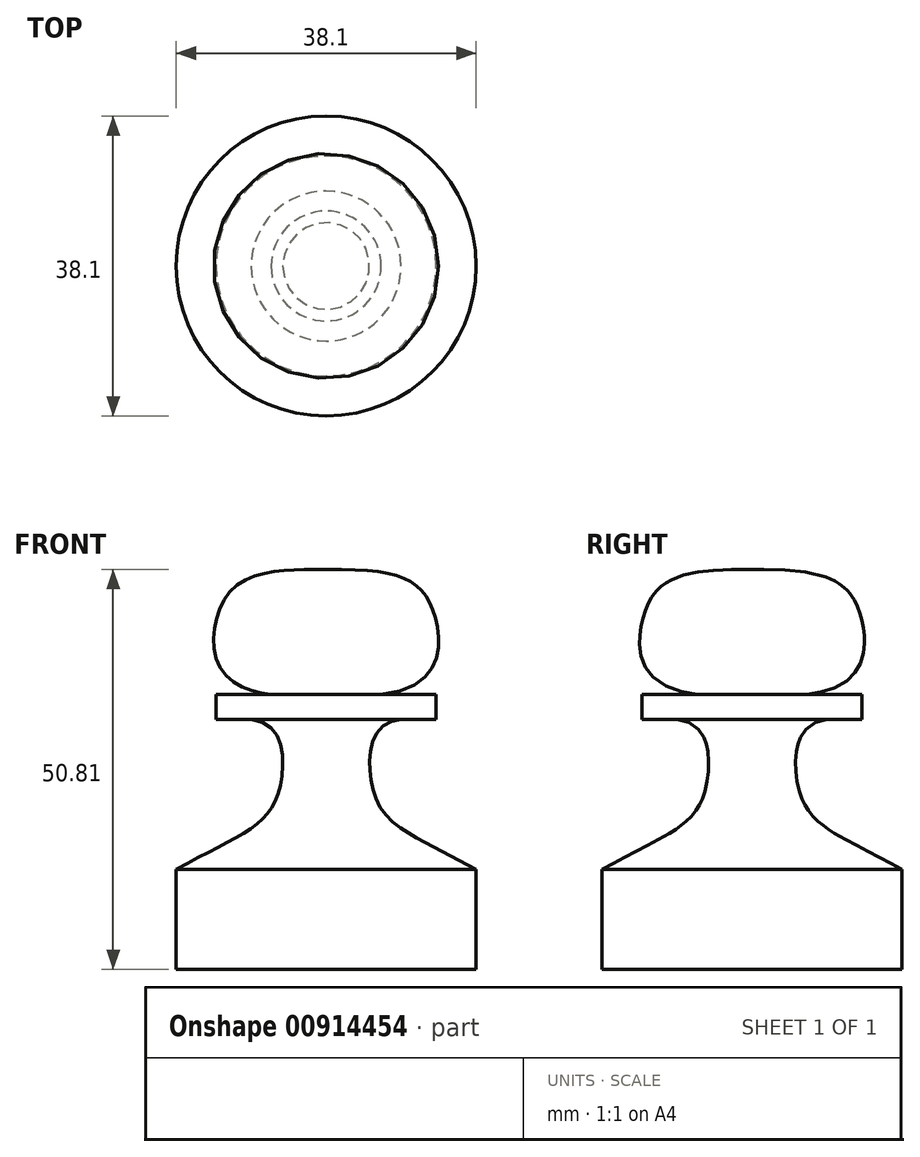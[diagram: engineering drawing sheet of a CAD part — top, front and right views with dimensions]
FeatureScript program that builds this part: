
annotation { "Feature Type Name" : "Feature", "Feature Type Description" : "" }
export const myFeature = defineFeature(function(context is Context, id is Id, definition is map)
    precondition{}
    {
        {
            var Q0;
            Q0=qCreatedBy(makeId("Front.planeOp"),FACE);
            var sketch = newSketch(context, id + "F0", { "sketchPlane" : qUnion([Q0])});
            skLineSegment(sketch, "E0", {"start": v(0, 0) * mm, "end": v(0, 50.8) * mm});
            skLineSegment(sketch, "E1", {"start": v(0, 0) * mm, "end": v(19.05, 0) * mm});
            skLineSegment(sketch, "E2", {"start": v(19.05, 0) * mm, "end": v(19.05, 12.7) * mm});
            skLineSegment(sketch, "E3", {"start": v(0, 31.75) * mm, "end": v(36.6, 31.75) * mm, "construction": true});
            skFitSpline(sketch, "E4", {"points": [v(19.05, 12.7) * mm, v(8.92, 18.38) * mm, v(5.75, 23.73) * mm, v(9.53, 31.75) * mm], "startDerivative": vector(-33.33, 18.75) * mm, "endDerivative": vector(37.53, 3.34) * mm});
            skLineSegment(sketch, "E5.bottom", {"start": v(0, 31.75) * mm, "end": v(13.97, 31.75) * mm});
            skLineSegment(sketch, "E5.top", {"start": v(0, 34.92) * mm, "end": v(13.97, 34.92) * mm});
            skLineSegment(sketch, "E5.left", {"start": v(0, 31.75) * mm, "end": v(0, 34.92) * mm});
            skLineSegment(sketch, "E5.right", {"start": v(13.97, 31.75) * mm, "end": v(13.97, 34.92) * mm});
            skFitSpline(sketch, "E6", {"points": [v(6.99, 34.92) * mm, v(13.98, 44.18) * mm, v(11.03, 49.05) * mm, v(0, 50.8) * mm], "startDerivative": vector(62.1, 7.27) * mm, "endDerivative": vector(-46.78, -0.83) * mm});
            skSolve(sketch);
        }
        {
            var Q0;
            {var subQ3=sQuery(id+"F0.wireOp",EDGE,"E6");Q0=makeQuery(id+"F0.imprint","IMPRINT",FACE,{"disambiguationData":[TD([[makeQuery(id+"F0.imprint","IMPRINT",EDGE,{"derivedFrom":subQ3}),1.0]])]});}
            var Q1;
            {var subQ2=sQuery(id+"F0.wireOp",EDGE,"E5.right");Q1=makeQuery(id+"F0.imprint","IMPRINT",FACE,{"disambiguationData":[TD([[makeQuery(id+"F0.imprint","IMPRINT",EDGE,{"derivedFrom":subQ2}),1.0]])]});}
            var Q2;
            {var subQ0=sQuery(id+"F0.wireOp",EDGE,"E1");Q2=makeQuery(id+"F0.imprint","IMPRINT",FACE,{"disambiguationData":[TD([[makeQuery(id+"F0.imprint","IMPRINT",EDGE,{"derivedFrom":subQ0}),1.0]])]});}
            var Q3;
            Q3=sQuery(id+"F0.wireOp",EDGE,"E0");
            revolve(context, id + "F1", {"surfaceOperationType" : NewSurfaceOperationType.NEW, "entities" : qUnion([Q0, Q1, Q2]), "axis" : qUnion([Q3]), "revolveType" : RevolveType.FULL});
        }
    });
